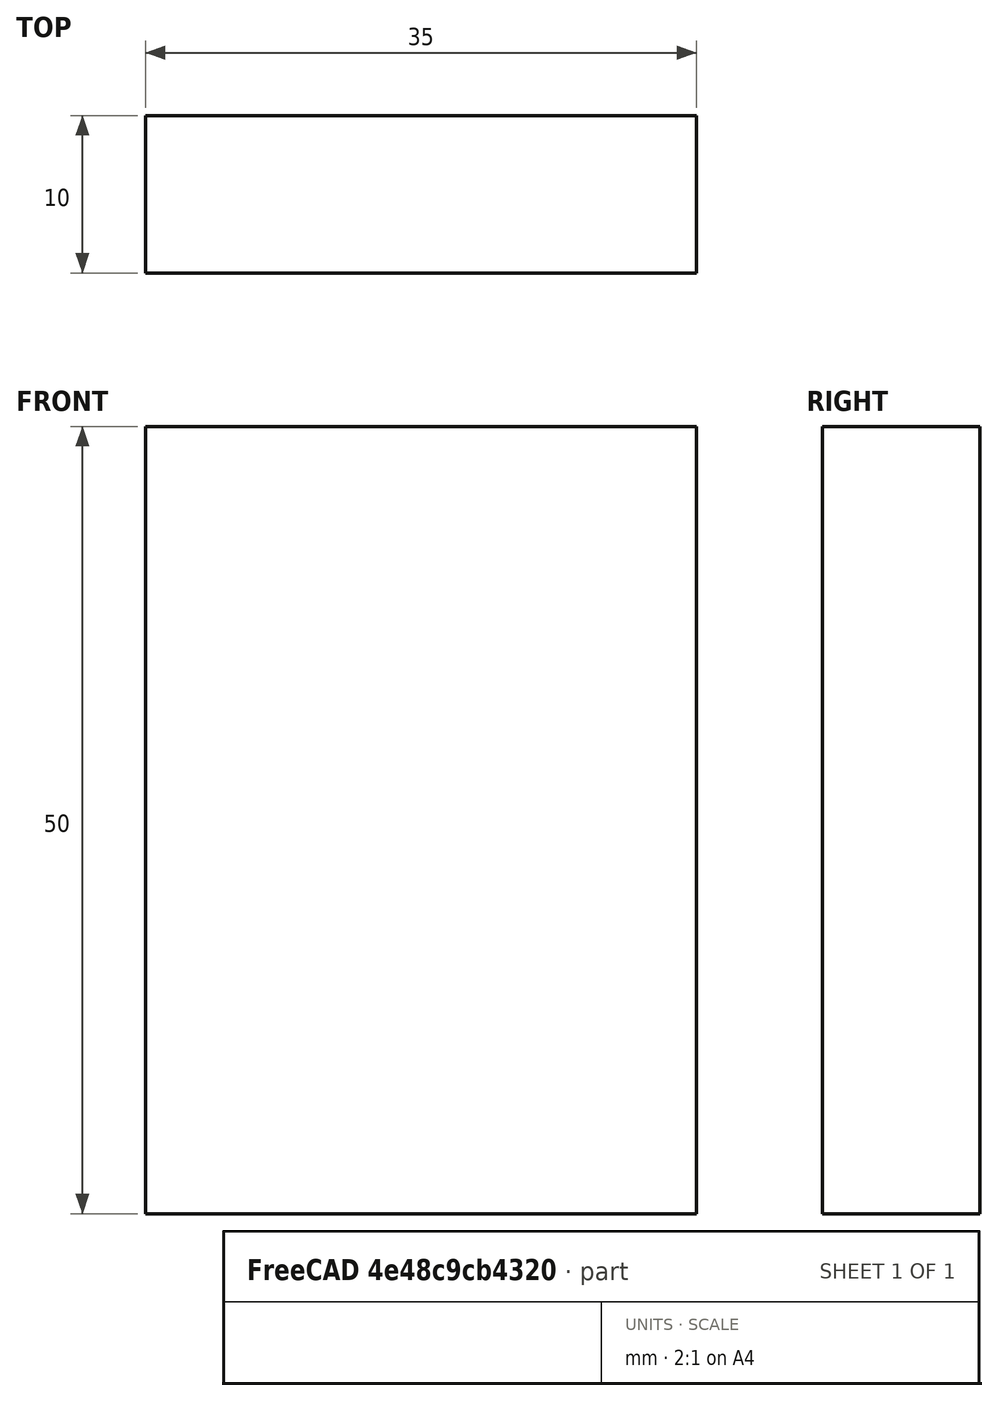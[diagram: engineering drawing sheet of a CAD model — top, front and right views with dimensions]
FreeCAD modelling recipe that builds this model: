
FCSTD DOCUMENT  (FreeCAD 0.15R4671 (Git))
Label: Flat Bar 35x10 EN10058 S235JR
License: All rights reserved
LicenseURL: http://en.wikipedia.org/wiki/All_rights_reserved
objects: Sketcher::SketchObject×1, Part::Extrusion×1
note: 2 computed .brp shape members not serialized (recipe doc carries the construction recipe); baked Part::Feature solids carry a one-line shape summary decoded from their .brp

FEATURE [Sketcher::SketchObject] Sketch
  sketch-geometry (4):
    g0: LineSegment StartX=-17.5 StartY=-5 StartZ=0 EndX=17.5 EndY=-5 EndZ=0
    g1: LineSegment StartX=17.5 StartY=-5 StartZ=0 EndX=17.5 EndY=5 EndZ=0
    g2: LineSegment StartX=17.5 StartY=5 StartZ=0 EndX=-17.5 EndY=5 EndZ=0
    g3: LineSegment StartX=-17.5 StartY=5 StartZ=0 EndX=-17.5 EndY=-5 EndZ=0
  constraints (12):
    c: Coincident(g0,g1)
    c: Coincident(g1,g2)
    c: Coincident(g2,g3)
    c: Coincident(g3,g0)
    c: Horizontal(g0)
    c: Horizontal(g2)
    c: Vertical(g1)
    c: Vertical(g3)
    c: Symmetric(g1,g2,g-2)
    c: Symmetric(g0,g1,g-1)
    c: DistanceY(g1) = 10
    c: DistanceX(g0) = 35
FEATURE [Part::Extrusion] Extrude  label="Flat Bar 35x10 EN10058 S235JR"
  Base = -> Sketch
  Dir = (0,0,50)
  Solid = true
